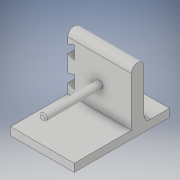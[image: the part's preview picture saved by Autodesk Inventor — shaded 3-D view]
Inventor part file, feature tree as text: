
AUTODESK INVENTOR PART (.ipt)
format: ipt  version: 2019 (Build 230136000, 136)  size: 155,136 bytes
history: native  units: in
note: dims shown in document units (in); Inventor stores cm internally (conversion verified against a paired STEP export)
features: fillet x4, extrude x3, sketch x3
ambient origin geometry x8: Origin, YZ Plane, XZ Plane, XY Plane, X Axis, Y Axis, Z Axis, Center Point
bodies: Solid1 (feature_tree)
feature tree (10):
  extrude  "Extrusion1"  Depth=1.9685in
  extrude  "Extrusion2"  Depth=0.1969in
  extrude  "Extrusion3"  Depth=0.0394in
  fillet  "Fillet1"  Radius=0.481in
  fillet  "Fillet2"  Radius=0.7953in
  fillet  "Fillet3"  Radius=0.2047in
  fillet  "Fillet4"  Radius=0.2047in
  sketch  "Sketch1"  dims[d0=1.9685in d1=1.9685in]
  sketch  "Sketch2"  dims[d2=1.9685in d5=0.481in d6=0.481in d7=0.1969in]
  sketch  "Sketch3"  dims[d8=0.4094in d9=0.481in d10=0.481in d11=0.7953in d12=0.2047in d13=0.2047in d14=0.4094in d15=1.5827in d16=0.481in d17=0.481in d18=0.2604in d19=0.2604in d21=0.3937in d22=0.0in d23=0.2205in d24=1.7717in d25=0.0in d26=0.5349in d27=0.7874in d28=0.0in d29=0.1969in d30=0.1969in d31=0.1969in d32=0.0394in]
